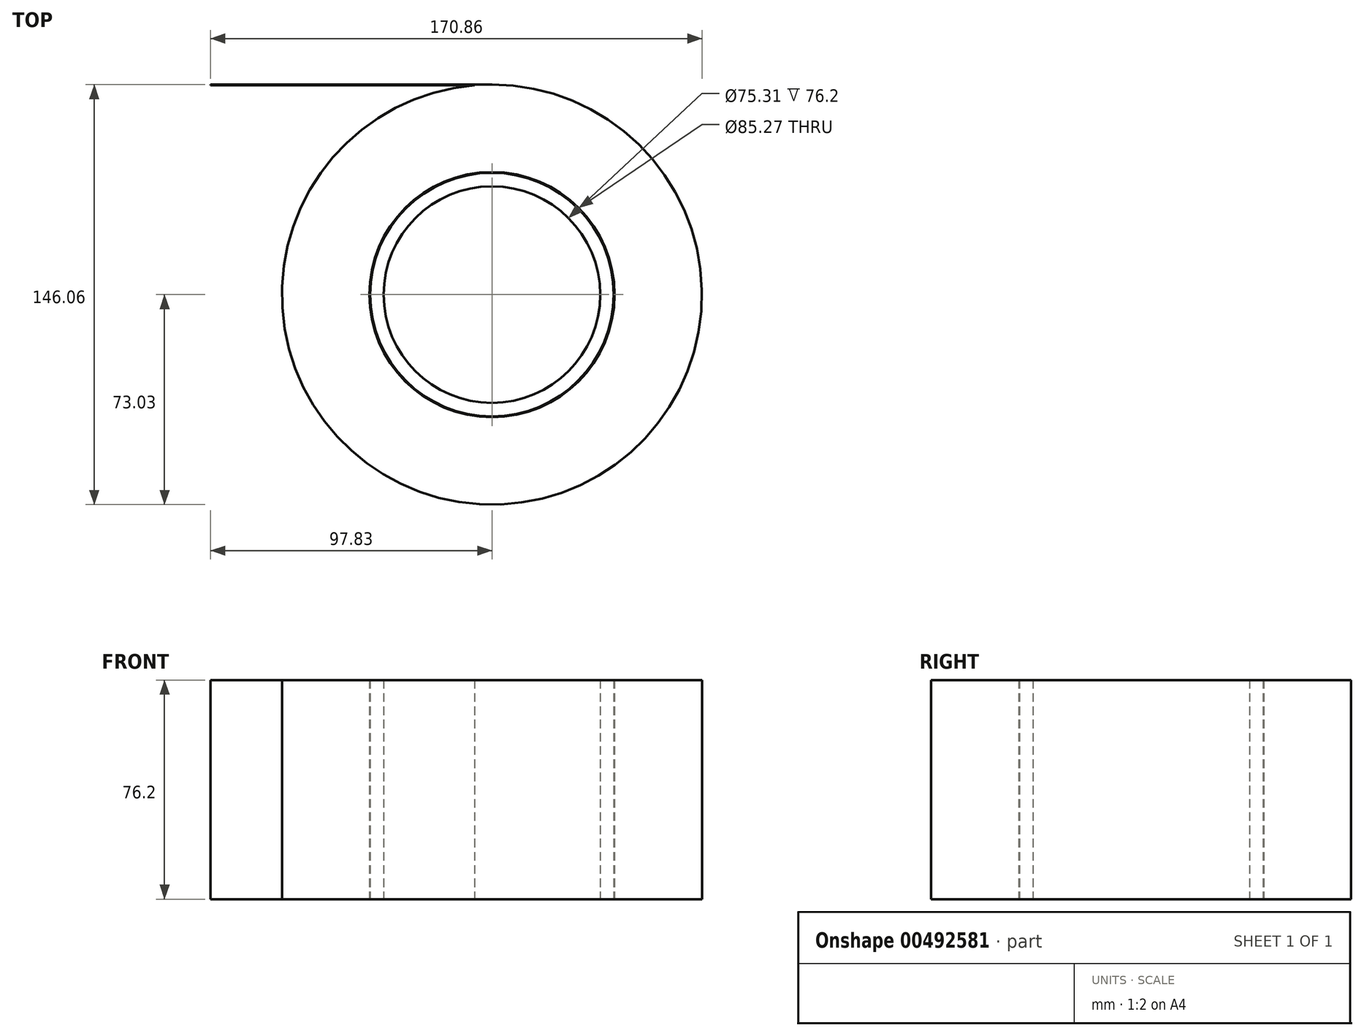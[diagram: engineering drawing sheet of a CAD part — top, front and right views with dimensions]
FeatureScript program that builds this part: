
annotation { "Feature Type Name" : "Feature", "Feature Type Description" : "" }
export const myFeature = defineFeature(function(context is Context, id is Id, definition is map)
    precondition{}
    {
        {
            var Q0;
            Q0=qCreatedBy(makeId("Top.planeOp"),FACE);
            var sketch = newSketch(context, id + "F0", { "sketchPlane" : qUnion([Q0])});
            skCircle(sketch, "E0", {"center": v(0, 0) * mm, "radius": 73.03 * mm});
            skCircle(sketch, "E1", {"center": v(0, 0) * mm, "radius": 42.64 * mm});
            skCircle(sketch, "E2", {"center": v(0, 0) * mm, "radius": 40.5 * mm});
            skSolve(sketch);
        }
        {
            var Q0;
            Q0=qSketchRegion(id+"F0",true);
            extrude(context, id + "F1", {"entities" : qUnion([Q0]), "depth" : 76.2 * mm});
        }
        {
            var Q0;
            Q0=qCreatedBy(makeId("Top.planeOp"),FACE);
            var sketch = newSketch(context, id + "F2", { "sketchPlane" : qUnion([Q0])});
            skCircle(sketch, "E3", {"center": v(0, 0) * mm, "radius": 37.66 * mm});
            skCircle(sketch, "E4", {"center": v(0, 0) * mm, "radius": 42.35 * mm});
            skSolve(sketch);
        }
        {
            var Q0;
            Q0=qSketchRegion(id+"F2",true);
            extrude(context, id + "F3", {"entities" : qUnion([Q0]), "depth" : 76.2 * mm});
        }
        {
            var Q0;
            Q0=qCreatedBy(makeId("Front.planeOp"),FACE);
            cPlane(context, id + "F4", {"entities" : qUnion([Q0]), "cplaneType" : CPlaneType.OFFSET, "offset" : 73.02 * mm, "oppositeDirection" : true, "width" : 152.4 * mm, "height" : 152.4 * mm});
        }
        {
            var Q0;
            Q0=qCreatedBy(id+"F4.planeOp",FACE);
            var sketch = newSketch(context, id + "F5", { "sketchPlane" : qUnion([Q0])});
            skLineSegment(sketch, "E5", {"start": v(0, 0) * mm, "end": v(-97.83, 0) * mm});
            skLineSegment(sketch, "E6.0", {"start": v(-73.03, 76.2) * mm, "end": v(0, 76.2) * mm});
            skLineSegment(sketch, "E7", {"start": v(0, 0) * mm, "end": v(0, 76.2) * mm});
            skLineSegment(sketch, "E8", {"start": v(-73.03, 76.2) * mm, "end": v(-97.83, 76.2) * mm});
            skLineSegment(sketch, "E9", {"start": v(-97.83, 76.2) * mm, "end": v(-97.83, 0) * mm});
            skPoint(sketch, "E10.orphan", {"position": v(73.03, 76.2) * mm});
            skSolve(sketch);
        }
        {
            var Q0;
            Q0=makeQuery(id+"F5.imprint","IMPRINT",FACE,{"disambiguationData":[TD([[makeQuery(id+"F5.imprint","IMPRINT",EDGE,{"derivedFrom":sQuery(id+"F5.wireOp",EDGE,"E5")}),-1.0]])]});
            extrude(context, id + "F6", {"entities" : qUnion([Q0]), "operationType" : NewBodyOperationType.ADD, "depth" : 0.25 * mm});
        }
    });
